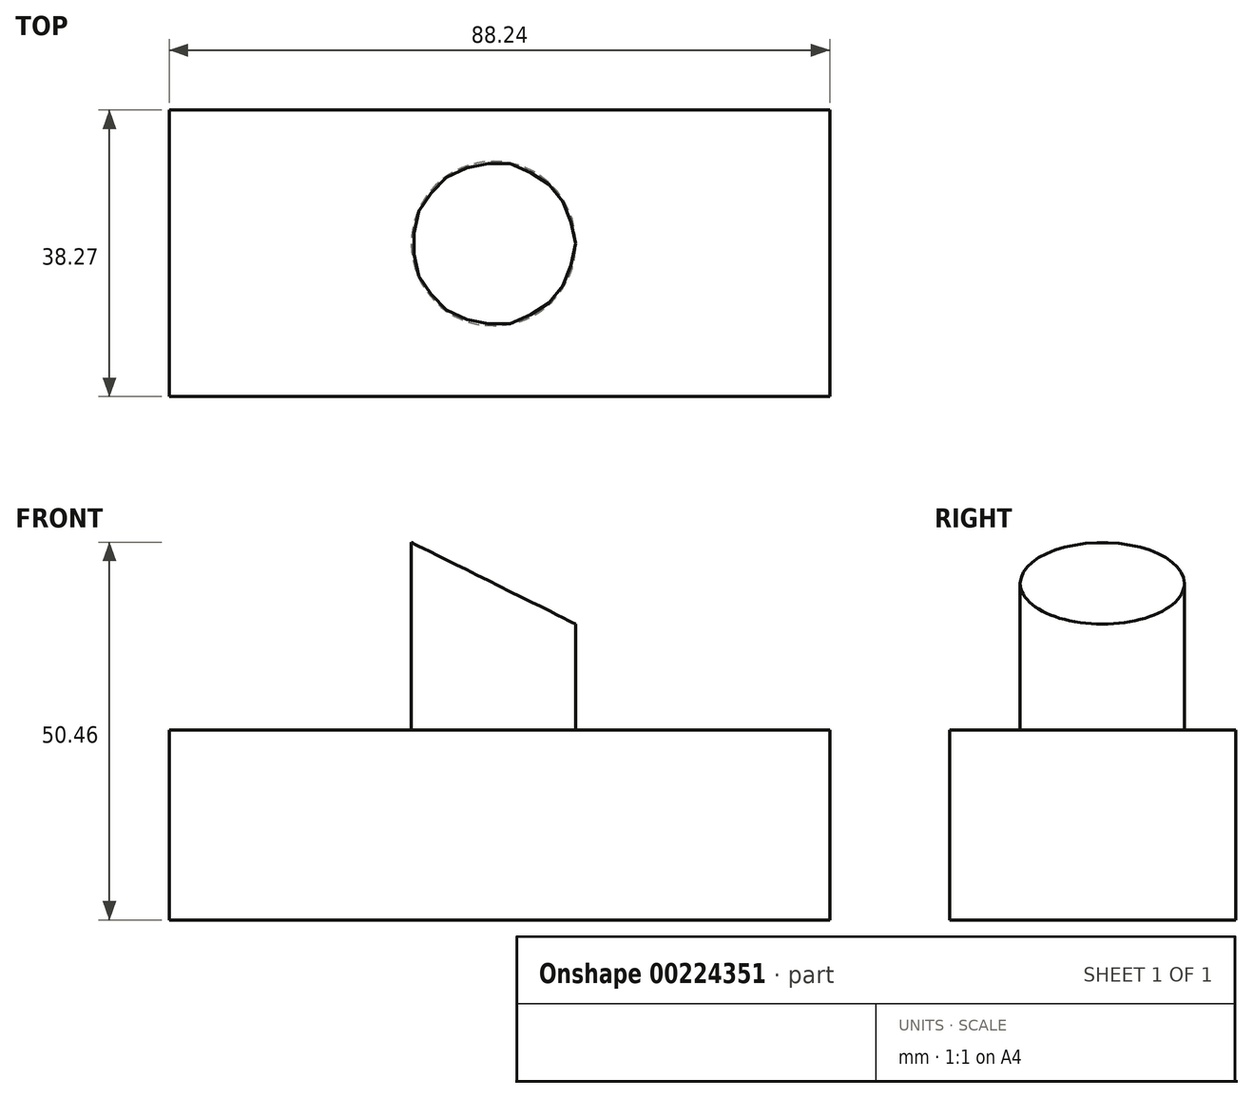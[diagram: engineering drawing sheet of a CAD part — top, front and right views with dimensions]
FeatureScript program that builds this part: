
annotation { "Feature Type Name" : "Feature", "Feature Type Description" : "" }
export const myFeature = defineFeature(function(context is Context, id is Id, definition is map)
    precondition{}
    {
        {
            var Q0;
            Q0=qCreatedBy(makeId("Top.planeOp"),FACE);
            var sketch = newSketch(context, id + "F0", { "sketchPlane" : qUnion([Q0])});
            skLineSegment(sketch, "E0.bottom", {"start": v(-43.32, 17.85) * mm, "end": v(44.92, 17.85) * mm});
            skLineSegment(sketch, "E0.top", {"start": v(-43.32, -20.42) * mm, "end": v(44.92, -20.42) * mm});
            skLineSegment(sketch, "E0.left", {"start": v(-43.32, 17.85) * mm, "end": v(-43.32, -20.42) * mm});
            skLineSegment(sketch, "E0.right", {"start": v(44.92, 17.85) * mm, "end": v(44.92, -20.42) * mm});
            skSolve(sketch);
        }
        {
            var Q0;
            Q0 = qSketchRegion(id + "F0", true);
            extrude(context, id + "F1", {"entities" : qUnion([Q0]), "depth" : 25.4 * mm});
        }
        {
            var Q0;
            Q0=makeQuery(id+"F1.opExtrude","CAP_FACE",FACE,{"disambiguationData":[OSD([sQuery(id+"F0.wireOp",EDGE,"E0.bottom"),sQuery(id+"F0.wireOp",EDGE,"E0.top"),sQuery(id+"F0.wireOp",EDGE,"E0.left"),sQuery(id+"F0.wireOp",EDGE,"E0.right")])],"isStart":false});
            var sketch = newSketch(context, id + "F2", { "sketchPlane" : qUnion([Q0])});
            skCircle(sketch, "E1", {"center": v(0, 0) * mm, "radius": 10.98 * mm});
            skSolve(sketch);
        }
        {
            var Q0;
            Q0=makeQuery(id+"F2.imprint","IMPRINT",FACE,{"disambiguationData":[TD([[makeQuery(id+"F2.imprint","IMPRINT",EDGE,{"derivedFrom":sQuery(id+"F2.wireOp",EDGE,"E1")}),1.0]])]});
            extrude(context, id + "F3", {"entities" : qUnion([Q0]), "operationType" : NewBodyOperationType.ADD, "depth" : 25.4 * mm});
        }
        {
            var Q0;
            Q0=qCreatedBy(makeId("Front.planeOp"),FACE);
            var sketch = newSketch(context, id + "F4", { "sketchPlane" : qUnion([Q0])});
            skLineSegment(sketch, "E2", {"start": v(-14.15, 55.87) * mm, "end": v(19.14, 55.87) * mm});
            skLineSegment(sketch, "E3", {"start": v(19.14, 55.87) * mm, "end": v(19.14, 35.48) * mm});
            skLineSegment(sketch, "E4", {"start": v(19.14, 35.48) * mm, "end": v(-18.52, 54.2) * mm});
            skLineSegment(sketch, "E5", {"start": v(-14.15, 55.87) * mm, "end": v(-18.52, 54.2) * mm});
            skSolve(sketch);
        }
        {
            var Q0;
            Q0=makeQuery(id+"F4.imprint","IMPRINT",FACE,{"disambiguationData":[TD([[makeQuery(id+"F4.imprint","IMPRINT",EDGE,{"derivedFrom":sQuery(id+"F4.wireOp",EDGE,"E2")}),-1.0]])]});
            extrude(context, id + "F5", {"entities" : qUnion([Q0]), "operationType" : NewBodyOperationType.REMOVE, "oppositeDirection" : true, "depth" : 25.4 * mm});
        }
        {
            var Q0;
            Q0 = qSketchRegion(id + "F4", true);
            extrude(context, id + "F6", {"entities" : qUnion([Q0]), "operationType" : NewBodyOperationType.REMOVE, "depth" : 25.4 * mm});
        }
    });
